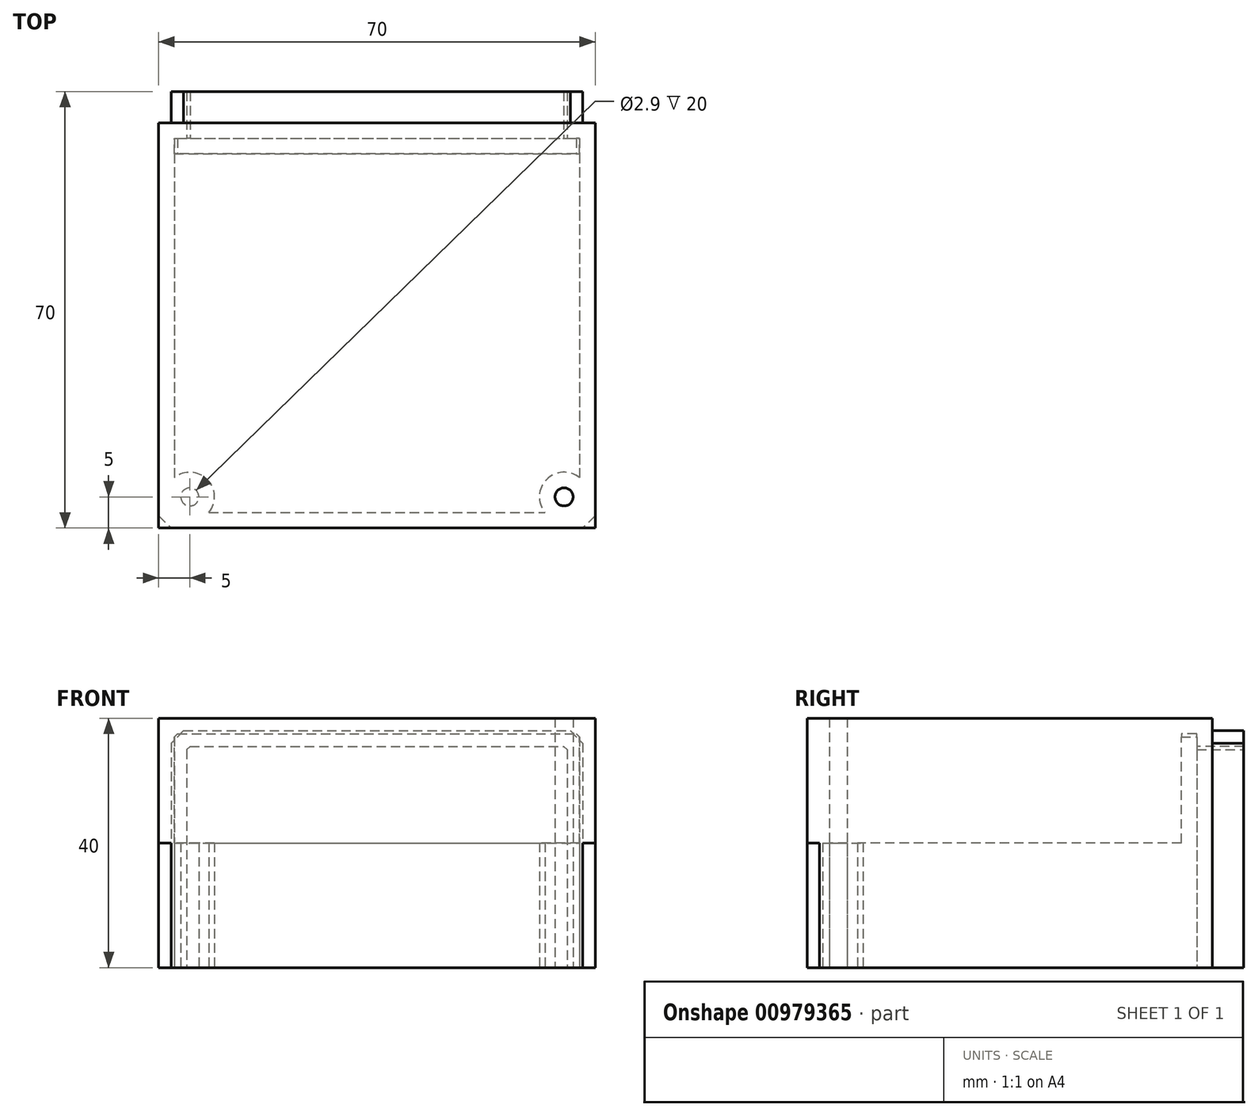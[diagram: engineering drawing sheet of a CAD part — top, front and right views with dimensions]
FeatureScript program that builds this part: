
annotation { "Feature Type Name" : "Feature", "Feature Type Description" : "" }
export const myFeature = defineFeature(function(context is Context, id is Id, definition is map)
    precondition{}
    {
        {
            var Q0;
            Q0=qCreatedBy(makeId("Top.planeOp"),FACE);
            var sketch = newSketch(context, id + "F0", { "sketchPlane" : qUnion([Q0])});
            skLineSegment(sketch, "E0.bottom", {"start": v(-35, 32.5) * mm, "end": v(35, 32.5) * mm});
            skLineSegment(sketch, "E0.top", {"start": v(-35, -32.5) * mm, "end": v(35, -32.5) * mm});
            skLineSegment(sketch, "E0.left", {"start": v(-35, 32.5) * mm, "end": v(-35, -32.5) * mm});
            skLineSegment(sketch, "E0.right", {"start": v(35, 32.5) * mm, "end": v(35, -32.5) * mm});
            skPoint(sketch, "E0.middle", {"position": v(0, 0) * mm});
            skLineSegment(sketch, "E1.bottom", {"start": v(-33, 37.5) * mm, "end": v(33, 37.5) * mm});
            skLineSegment(sketch, "E1.top", {"start": v(-33, 27.5) * mm, "end": v(33, 27.5) * mm});
            skLineSegment(sketch, "E1.left", {"start": v(-33, 37.5) * mm, "end": v(-33, 27.5) * mm});
            skLineSegment(sketch, "E1.right", {"start": v(33, 37.5) * mm, "end": v(33, 27.5) * mm});
            skCircle(sketch, "E2", {"center": v(-30, -27.5) * mm, "radius": 1.45 * mm});
            skCircle(sketch, "E3.MirrorC", {"center": v(30, -27.5) * mm, "radius": 1.45 * mm});
            skLineSegment(sketch, "E4", {"start": v(-30, -27.5) * mm, "end": v(30, -27.5) * mm, "construction": true});
            skSolve(sketch);
        }
        {
            var Q0;
            Q0=makeQuery(id+"F0.imprint","IMPRINT",FACE,{"disambiguationData":[TD([[makeQuery(id+"F0.imprint","IMPRINT",EDGE,{"derivedFrom":sQuery(id+"F0.wireOp",EDGE,"E0.top")}),1.0]])]});
            var Q1;
            {var subQ5=sQuery(id+"F0.wireOp",EDGE,"E1.top");Q1=makeQuery(id+"F0.imprint","IMPRINT",FACE,{"disambiguationData":[TD([[makeQuery(id+"F0.imprint","IMPRINT",EDGE,{"derivedFrom":subQ5}),1.0]])]});}
            extrude(context, id + "F1", {"entities" : qUnion([Q0, Q1]), "depth" : 40 * mm, "offsetDistance" : 25 * mm});
        }
        {
            var Q0;
            Q0 = qSketchRegion(id + "F0", true);
            extrude(context, id + "F2", {"entities" : qUnion([Q0]), "operationType" : NewBodyOperationType.ADD, "depth" : 38 * mm, "offsetDistance" : 25 * mm});
        }
        {
            var Q0;
            Q0=makeQuery(id+"F1.opExtrude","CAP_EDGE",EDGE,{"disambiguationData":[OSD([sQuery(id+"F0.wireOp",EDGE,"E0.top")])],"isStart":false});
            var Q1;
            Q1=makeQuery(id+"F1.opExtrude","CAP_EDGE",EDGE,{"disambiguationData":[OSD([sQuery(id+"F0.wireOp",EDGE,"E0.right")])],"isStart":false});
            var Q2;
            Q2=makeQuery(id+"F1.opExtrude","CAP_EDGE",EDGE,{"disambiguationData":[OSD([sQuery(id+"F0.wireOp",EDGE,"E0.left")])],"isStart":false});
            var Q3;
            Q3=makeQuery(id+"F2.opExtrude","CAP_EDGE",EDGE,{"disambiguationData":[OSD([sQuery(id+"F0.wireOp",EDGE,"E1.right")])],"isStart":false});
            var Q4;
            Q4=makeQuery(id+"F2.opExtrude","CAP_EDGE",EDGE,{"disambiguationData":[OSD([sQuery(id+"F0.wireOp",EDGE,"E1.left")])],"isStart":false});
            var Q5;
            Q5=makeQuery(id+"F1.opExtrude","SWEPT_EDGE",EDGE,{"disambiguationData":[OSD([sQuery(id+"F0.wireOp",EDGE,"E0.top"),sQuery(id+"F0.wireOp",EDGE,"E0.left")])]});
            var Q6;
            Q6=makeQuery(id+"F1.opExtrude","SWEPT_EDGE",EDGE,{"disambiguationData":[OSD([sQuery(id+"F0.wireOp",EDGE,"E0.top"),sQuery(id+"F0.wireOp",EDGE,"E0.right")])]});
            chamfer(context, id + "F3", {"entities" : qUnion([Q0, Q1, Q2, Q3, Q4, Q5, Q6]), "width" : 2 * mm, "tangentPropagation" : true});
        }
        {
            var Q0;
            {var subQ0=sQuery(id+"F0.wireOp",EDGE,"E0.right");var subQ1=sQuery(id+"F0.wireOp",EDGE,"E0.left");var subQ2=sQuery(id+"F0.wireOp",EDGE,"E0.top");var subQ3=sQuery(id+"F0.wireOp",EDGE,"E0.bottom");Q0=makeQuery(id+"F2.boolean.opBoolean","MERGE",FACE,{"derivedFrom":[makeQuery(id+"F1.opExtrude","CAP_FACE",FACE,{"disambiguationData":[OSD([subQ3,subQ2,subQ1,subQ0])],"isStart":true}),makeQuery(id+"F2.opExtrude","CAP_FACE",FACE,{"disambiguationData":[OSD([subQ3,subQ2,subQ1,subQ0,sQuery(id+"F0.wireOp",EDGE,"E1.bottom"),sQuery(id+"F0.wireOp",EDGE,"E1.left"),sQuery(id+"F0.wireOp",EDGE,"E1.right")])],"isStart":true})]});}
            var Q1;
            Q1=makeQuery(id+"F2.opExtrude","SWEPT_FACE",FACE,{"disambiguationData":[OSD([sQuery(id+"F0.wireOp",EDGE,"E1.bottom")])]});
            shell(context, id + "F4", {"entities" : qUnion([Q0, Q1]), "thickness" : 2.5 * mm});
        }
        {
            var Q0;
            Q0=makeQuery(id+"F0.imprint","IMPRINT",FACE,{"disambiguationData":[TD([[makeQuery(id+"F0.imprint","IMPRINT",EDGE,{"derivedFrom":sQuery(id+"F0.wireOp",EDGE,"E2")}),1.0]])]});
            var Q1;
            Q1=makeQuery(id+"F0.imprint","IMPRINT",FACE,{"disambiguationData":[TD([[makeQuery(id+"F0.imprint","IMPRINT",EDGE,{"derivedFrom":sQuery(id+"F0.wireOp",EDGE,"E3.MirrorC")}),-1.0]])]});
            var Q2;
            Q2=makeQuery(id+"F1.opExtrude","CAP_FACE",FACE,{"disambiguationData":[OSD([sQuery(id+"F0.wireOp",EDGE,"E0.bottom"),sQuery(id+"F0.wireOp",EDGE,"E0.top"),sQuery(id+"F0.wireOp",EDGE,"E0.left"),sQuery(id+"F0.wireOp",EDGE,"E0.right"),sQuery(id+"F0.wireOp",EDGE,"E2"),sQuery(id+"F0.wireOp",EDGE,"E3.MirrorC")])],"isStart":false});
            var Q3;
            Q3=makeQuery(id+"F1.opExtrude","CAP_FACE",FACE,{"disambiguationData":[OSD([sQuery(id+"F0.wireOp",EDGE,"E0.bottom"),sQuery(id+"F0.wireOp",EDGE,"E0.top"),sQuery(id+"F0.wireOp",EDGE,"E0.left"),sQuery(id+"F0.wireOp",EDGE,"E0.right"),sQuery(id+"F0.wireOp",EDGE,"E2"),sQuery(id+"F0.wireOp",EDGE,"E3.MirrorC")])],"isStart":false});
            extrude(context, id + "F5", {"entities" : qUnion([Q0, Q1]), "operationType" : NewBodyOperationType.ADD, "depth" : 40 * mm, "endBoundEntityFace" : qUnion([Q2]), "hasOffset" : true, "offsetDistance" : 30 * mm, "offsetOppositeDirection" : true, "hasSecondDirection" : true, "secondDirectionOppositeDirection" : false, "secondDirectionDepth" : 20 * mm, "secondDirectionBoundEntityFace" : qUnion([Q3])});
        }
    });
